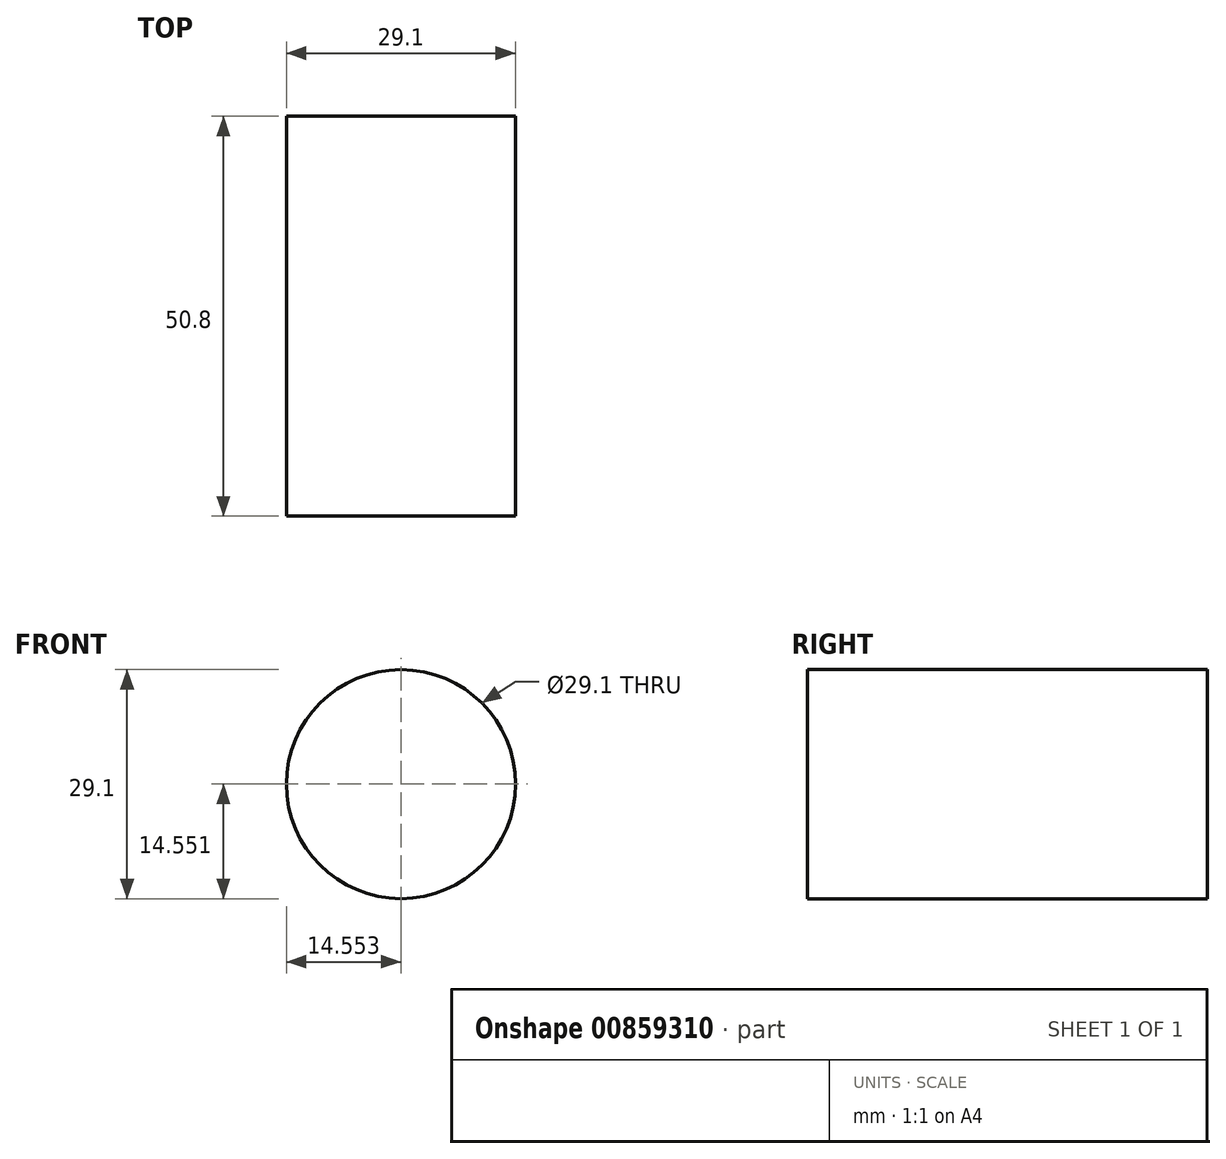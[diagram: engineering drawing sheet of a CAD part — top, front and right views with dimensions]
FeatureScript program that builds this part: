
annotation { "Feature Type Name" : "Feature", "Feature Type Description" : "" }
export const myFeature = defineFeature(function(context is Context, id is Id, definition is map)
    precondition{}
    {
        {
            var Q0;
            Q0=qCreatedBy(makeId("Front.planeOp"),FACE);
            var sketch = newSketch(context, id + "F0", { "sketchPlane" : qUnion([Q0])});
            skCircle(sketch, "E0", {"center": v(-5.77, 0) * mm, "radius": 26.95 * mm});
            skCircle(sketch, "E1", {"center": v(-31.4, 0.36) * mm, "radius": 14.55 * mm});
            skSolve(sketch);
        }
        {
            var Q0;
            Q0=sQuery(id+"F0.wireOp",EDGE,"E1");
            extrude(context, id + "F1", {"bodyType" : ToolBodyType.SURFACE, "surfaceEntities" : qUnion([Q0]), "oppositeDirection" : true, "depth" : 25.4 * mm, "offsetDistance" : 25.4 * mm, "hasSecondDirection" : true, "secondDirectionOppositeDirection" : false, "secondDirectionDepth" : 25.4 * mm});
        }
    });
